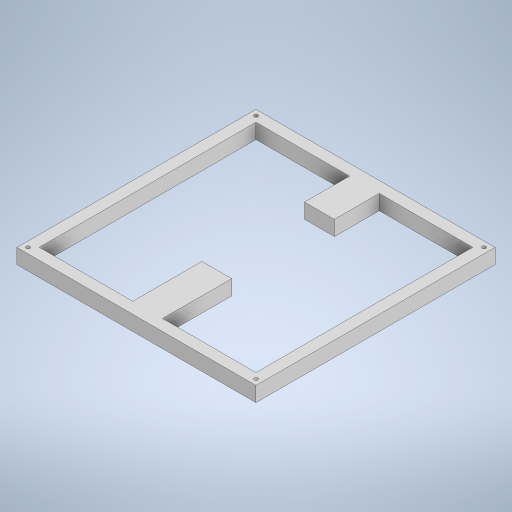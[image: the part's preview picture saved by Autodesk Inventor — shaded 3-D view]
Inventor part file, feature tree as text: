
AUTODESK INVENTOR PART (.ipt)
format: ipt  version: 2023 (Build 270158000, 158)  size: 293,376 bytes
history: native  units: in
note: dims shown in document units (in); Inventor stores cm internally (conversion verified against a paired STEP export)
features: sketch x3, extrude x2, projected_geometry x2
ambient origin geometry x8: Origin, YZ Plane, XZ Plane, XY Plane, X Axis, Y Axis, Z Axis, Center Point
bodies: Solid1 (feature_tree)
feature tree (7):
  extrude  "Extrusion1"  Depth=4.0in
  extrude  "Extrusion2"  Depth=0.25in TaperAngle=0.0deg
  sketch  "Sketch3"  dims[d13=0.5in d15=1.1562in d16=0.5in d17=0.9063in d18=0.25in d20=0.0625in d21=0.0938in d22=0.0938in d23=0.7874in d25=3.8125in d26=0.7874in d28=3.8125in d31=0.25in d32=0.0in d33=0.75in d34=0.0344in d35=0.5in d36=0.0344in]
  sketch  "Sketch1"  dims[d0=4.0in d1=4.0in]
  sketch  "Sketch2"  dims[d2=0.1875in d11=0.25in d12=0.0in]
  projected_geometry  "Projected Loop1"
  projected_geometry  "Projected Loop2"
